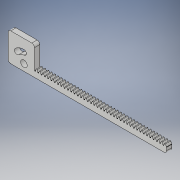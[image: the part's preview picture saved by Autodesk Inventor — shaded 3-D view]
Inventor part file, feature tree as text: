
AUTODESK INVENTOR PART (.ipt)
format: ipt  version: 2019 (Build 230136000, 136)  size: 340,992 bytes
history: native  units: in
note: dims shown in document units (in); Inventor stores cm internally (conversion verified against a paired STEP export)
features: extrude x3, sketch x2, pattern_linear x1, fillet x1
ambient origin geometry x8: Origin, YZ Plane, XZ Plane, XY Plane, X Axis, Y Axis, Z Axis, Center Point
bodies: Solid1 (feature_tree)
feature tree (7):
  extrude  "Extrusion1"  Depth=0.8474in
  extrude  "Extrusion2"  Depth=0.2362in
  extrude  "Extrusion4"  Depth=0.2362in
  pattern_linear  "Rectangular Pattern1"  Spacing1=0.5906in  [1 undecoded]
  fillet  "Fillet1"  Radius=0.4724in
  sketch  "Sketch1"  dims[d0=0.1575in d1=0.0in d3=0.8474in]
  sketch  "Sketch2"  dims[d4=0.1969in d5=0.1495in d7=0.1495in d8=0.5906in d9=0.4724in d10=0.1575in d11=0.0in d12=0.0787in d26=4.7244in d49=0.3937in d50=0.0in d53=15.748in d55=0.0982in d57=0.1969in d58=0.0071in d59=0.0708in d60=0.0104in d61=0.0263in d62=0.0878in d64=0.7874in d66=0.2362in]
note: 1 required parameter value undecoded (feature->parameter linkage not recoverable at this tier; creation-order binding heuristic only, values carry confidence <= 0.55)
